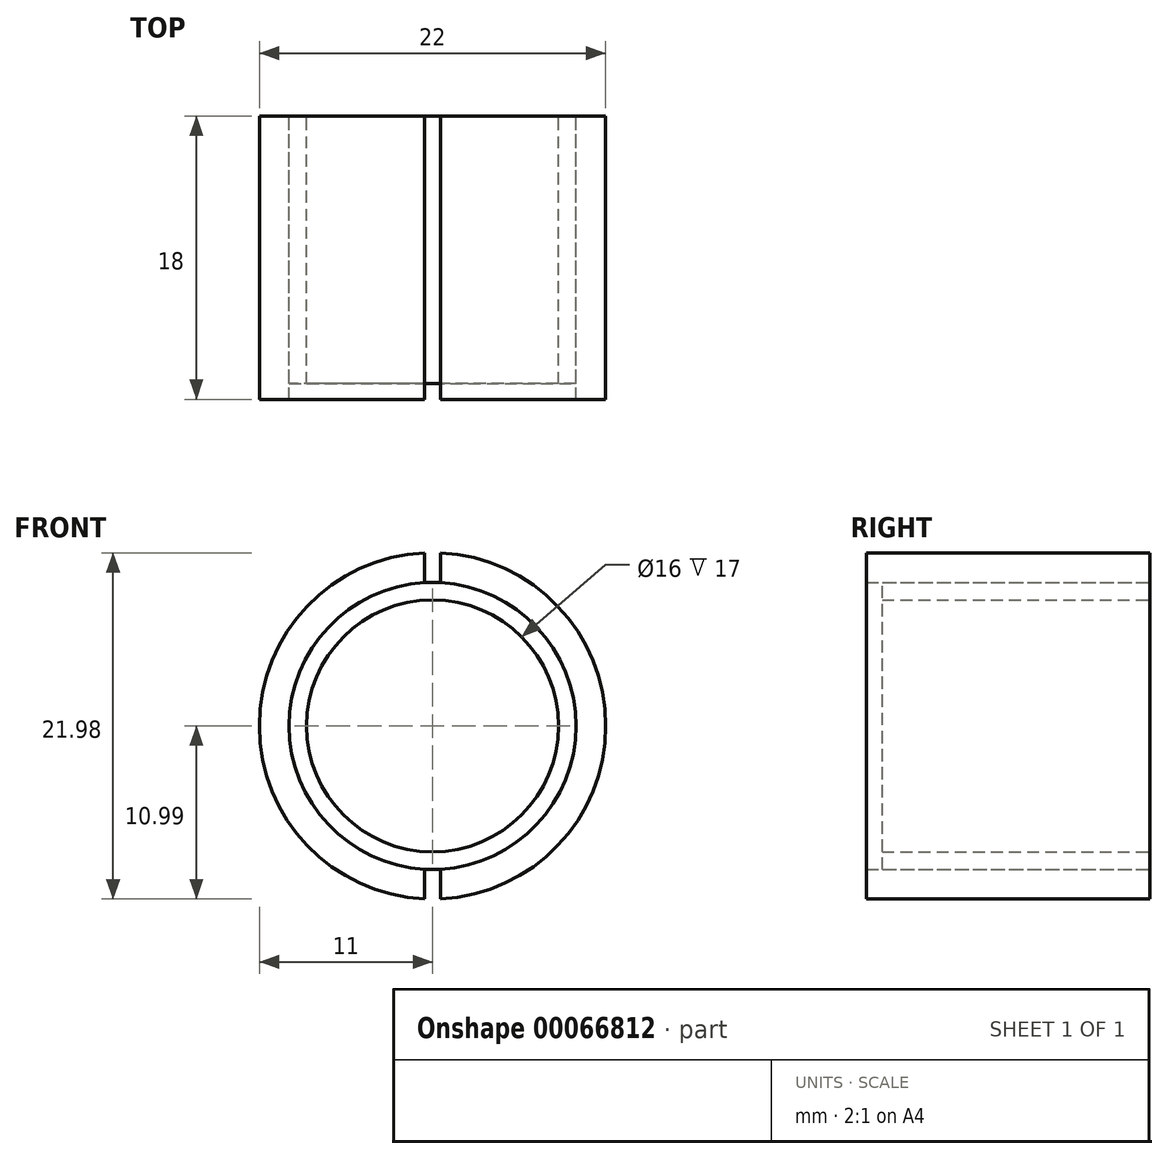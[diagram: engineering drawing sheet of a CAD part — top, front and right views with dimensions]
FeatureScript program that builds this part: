
annotation { "Feature Type Name" : "Feature", "Feature Type Description" : "" }
export const myFeature = defineFeature(function(context is Context, id is Id, definition is map)
    precondition{}
    {
        {
            var Q0;
            Q0=qCreatedBy(makeId("Front.planeOp"),FACE);
            var sketch = newSketch(context, id + "F0", { "sketchPlane" : qUnion([Q0])});
            skCircle(sketch, "E0", {"center": v(0, 0) * mm, "radius": 11 * mm});
            skCircle(sketch, "E1", {"center": v(0, 0) * mm, "radius": 8 * mm});
            skCircle(sketch, "E2", {"center": v(0, 0) * mm, "radius": 11.5 * mm});
            skCircle(sketch, "E3", {"center": v(0, 0) * mm, "radius": 9.11 * mm});
            skSolve(sketch);
        }
        {
            var Q0;
            Q0=makeQuery(id+"F0.imprint","IMPRINT",FACE,{"disambiguationData":[TD([[makeQuery(id+"F0.imprint","IMPRINT",EDGE,{"derivedFrom":sQuery(id+"F0.wireOp",EDGE,"E0")}),1.0]])]});
            extrude(context, id + "F1", {"entities" : qUnion([Q0]), "depth" : 18 * mm});
        }
        {
            var Q0;
            Q0=qCreatedBy(makeId("Front.planeOp"),FACE);
            var sketch = newSketch(context, id + "F2", { "sketchPlane" : qUnion([Q0])});
            skLineSegment(sketch, "E4", {"start": v(-0.5, 1.3) * mm, "end": v(-0.5, 11.3) * mm});
            skLineSegment(sketch, "E5", {"start": v(-0.5, 11.3) * mm, "end": v(0.5, 11.28) * mm});
            skLineSegment(sketch, "E6", {"start": v(0.5, 11.28) * mm, "end": v(0.5, 1.3) * mm});
            skLineSegment(sketch, "E7", {"start": v(0.5, 1.3) * mm, "end": v(-0.5, 1.3) * mm});
            skLineSegment(sketch, "E8.MirrorCS", {"start": v(-0.5, -1.3) * mm, "end": v(-0.5, -11.3) * mm});
            skLineSegment(sketch, "E9.MirrorCS", {"start": v(0.5, -11.28) * mm, "end": v(0.5, -1.3) * mm});
            skLineSegment(sketch, "E10", {"start": v(0.5, -1.3) * mm, "end": v(-0.5, -1.3) * mm});
            skLineSegment(sketch, "E11", {"start": v(0.5, -11.28) * mm, "end": v(-0.5, -11.3) * mm});
            skSolve(sketch);
        }
        {
            var Q0;
            Q0=makeQuery(id+"F2.imprint","IMPRINT",FACE,{"disambiguationData":[TD([[makeQuery(id+"F2.imprint","IMPRINT",EDGE,{"derivedFrom":sQuery(id+"F2.wireOp",EDGE,"E4")}),-1.0]])]});
            var Q1;
            Q1=makeQuery(id+"F2.imprint","IMPRINT",FACE,{"disambiguationData":[TD([[makeQuery(id+"F2.imprint","IMPRINT",EDGE,{"derivedFrom":sQuery(id+"F2.wireOp",EDGE,"E8.MirrorCS")}),1.0]])]});
            extrude(context, id + "F3", {"entities" : qUnion([Q0, Q1]), "operationType" : NewBodyOperationType.REMOVE, "depth" : 25 * mm});
        }
        {
            var Q0;
            Q0=makeQuery(id+"F0.imprint","IMPRINT",FACE,{"disambiguationData":[TD([[makeQuery(id+"F0.imprint","IMPRINT",EDGE,{"derivedFrom":sQuery(id+"F0.wireOp",EDGE,"E1")}),-1.0]])]});
            extrude(context, id + "F4", {"entities" : qUnion([Q0]), "depth" : 17 * mm});
        }
    });
